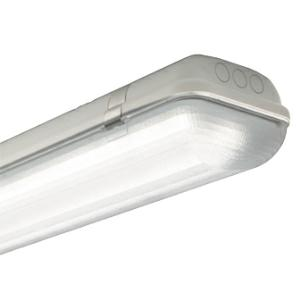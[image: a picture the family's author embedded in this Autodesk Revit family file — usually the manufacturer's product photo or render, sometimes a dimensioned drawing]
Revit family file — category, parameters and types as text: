
# Revit family: 3f_filippi_-_3f_linda_3f_filippi_-_58625_-_3f_linda_led_2x30w-830_ep_l1570
name_source: partatom
category: Lighting Fixtures
units: mm (PartAtom-declared; Revit-internal decimal feet)

## family parameters
Cut with Voids When Loaded = No
Host = Face
Light Source = No
Part Type = Normal
Room Calculation Point = No
Round Connector Dimension = Use Diameter
Shared = No

## types (1)
- 3F Filippi - 3F Linda (1 x LED, 9230 lm, 67 W, 3000 K)
    Apparent Load = 67 VA
    Approval mark = ENEC
    CIE Flux Codes = 46 76 93 97 100
    Color Rendering = 80
    Color Temperature = 3000 K
    Control Gear = Electronic ballast
    Default Elevation = 1800 mm
    Description = ILLUMINOTECHNICAL
Luminous efficiency 100% (DLOR 97%, ULOR 3%).
Initial luminous flux of the luminaire 9230 lm.
Emergency luminaire luminous flux BLF 5.7%.
Controlled symmetric distribution.
Installation Interdistance Transv.D = 1.52 x hu - Long.D = 1.17 x hu.
Tabular UGR (CIE 117 - 4H-8H; S=0.25H; 70/50/20): RUG 24.2 - 23.4.
Beam angle: 94° - 78°.
Luminous efficacy 138 lm/W.
Lifetime (L93/B10): 30000 h. (tq+25°C)
Lifetime (L90/B10): 50000 h. (tq+25°C)
Lifetime (L85/B10): 80000 h. (tq+25°C)
Lifetime (L80/B10): 100000 h. (tq+25°C)
Sudden decreased luminous flux after 50000 hours: 0% (C0).
Photobiological safety in compliance with IEC/TR 62778: RG0 risk exempt, (IEC 62471).
In compliance with IEC/EN 62722-2-1 - IEC/EN 62717 standards.

SOURCE
2 linear LED modules 30W/830.
Energy efficiency class (UE 2019/2020 - UE 2019/2015): D.
CIE 13.3 Colour rendering index: CRI >80 (R9 <50%).
IES TM-30 Fidelity Index: Rf = 84 Rg = 95.
CCT nominal colour temperature 3000 K.
Colour initial tolerance (MacAdam): SDCM 3.

MECHANICAL
Self-extinguishing V2 polycarbonate housing, injection moulded, RAL 7035 grey.
Ecologic anti-aging injected sealing gasket.
Diffuser in self-extinguishing V2 polycarbonate, photo-engraved interior, UV stabilised, injection moulded with smooth outer surface, tamper-proof opening.
Gear-holder reflector in hot-dip galvanised steel, painted with white polyester base.
Snug fit safety snap-lock clips for diffuser mounting in stainless steel, screwdriver opening.
Fixing brackets in stainless steel.
Possibility for technicians to access the interior of the luminaire.
Luminaire with limited surface temperature. - D - (EN 60598-2-24)
Dimensions: 1570x160 mm, height 100 mm. Weight 3.895 kg.
IP66 protection degree.
Mechanical strength to impacts IK10 (20 joule).
Glow-wire test resistance 850°C.

ELECTRICAL
Halogen Free electronic wiring 230V-50/60Hz, power factor 0.90, THD <25%, constant output current, SELV, class I, 1 driver.
Power of the luminaire 67 W.
CE - IEC 60598-1 - EN 60598-1.
EP maintained emergency wiring on board, 1h duration, 24h recharge; compliant with EN 60598-2-22, excluding high risk areas.
SAFE FLICKER: PstLM=<1 and SVM=<0.4 (IEC TR 61547-1 and IEC TR 63158), to ensure a more comfortable and safe light.
Ambient temperature from +5°C to +25°C.
Temperature class T6 max 85°C.
Relative humidity UR: <85%.

INSTALLATION
Ceiling / Suspended / Wall.
All accessories dedicated to this product are available on the Catalog and on our website www.3F-Filippi.com.

APPLICATIONS
Suitable product for food production plants (HACCP), IFS (Food Version 6), BRC (GSFS Food Version 7).
Dry, dusty indoor environments, subject to occasional water splashes.
Virtually shatterproof polycarbonate compatibly with the fumes / atmospheres that compromise the elasticity of plastic materials.
Not suitable for installation on surfaces subject to important vibrations, exposed to weather conditions, on ropes or poles.
Suitable for illumination of public car parks and parking grounds referred to DIN 67528:2018-04.

WARNING
Fixture not suitable for cold stores with an ambient temperature <5°C and/or relative humidity >85%.
Luminaire designed for disposal/recycling at end-of-life.
Replaceable (LED only) light source by a professional. Replaceable control gear by a professional.
    Height = 100 mm  [stored 0.328084 ft]
    Lamp = 1 x LED
    Lamp Light Flux = 9230 lm
    Lamp Power = 67 W
    Lamp count = 1
    Length = 1570 mm
    Lifetime = 50000 h
    Luminous efficacy = 138 lm/W
    Manufacturer = 3F Filippi
    ModVariant = No
    Model = 3F Filippi - 58625 - 3F Linda LED 2x30W-830 EP L1570
    Mounting Place = Ceiling
    Mounting Type = Pendant
    Number of Poles = 1
    OnlyDefault = Yes
    Power Factor = 1
    Product Name = 3F Filippi - 3F Linda
    Product group = pendant luminaire
    ProductGroupID = 9
    Protection Class = Protection class I
    Protection Degree = IP 66
    RLX_Detail_Level = 1
    RLX_Emergency_Light_Flux = 0 lm
    RLX_Emergency_Type = 0
    RLX_Emergency_Type_DB = No
    RlxData = <blob elided: 72293 chars, md5=207d136e>
    Socket = socket
    Standby Power = 0 W
    System Light Flux = 9230 lm
    System Power = 67 W
    Type Comments = Product without accessories
    Type Image = 3ffilippi_58625.jpg
    URL = http://relux.com
    VarID = ---
    Voltage = 0 V
    Weight = 0.00 kg
    Width = 160 mm

note: [stored X ft] marks values corroborated as IEEE doubles in the binary element streams (Revit-internal decimal feet)

## geometry (parser evidence)
native form markers: Blend x4, Sweep x10
no freeform markers — native parametric forms only
